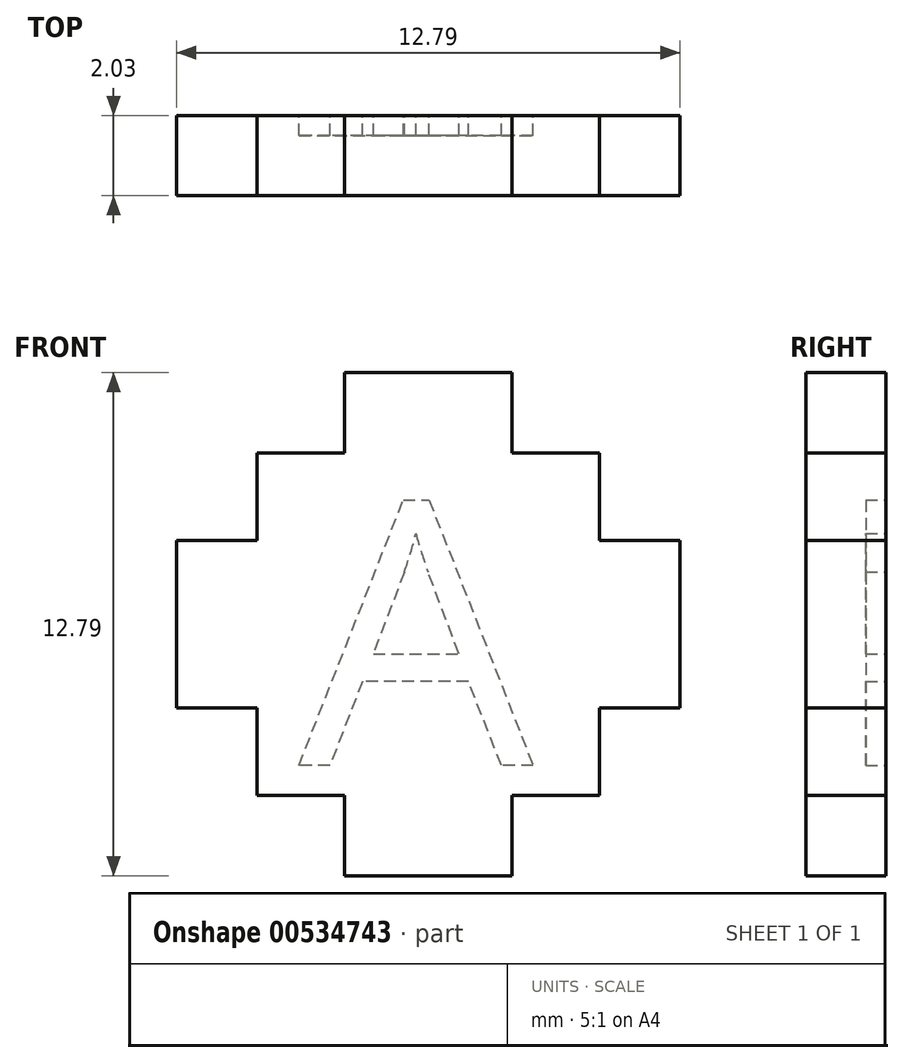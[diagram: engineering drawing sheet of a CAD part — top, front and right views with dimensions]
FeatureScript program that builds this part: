
annotation { "Feature Type Name" : "Feature", "Feature Type Description" : "" }
export const myFeature = defineFeature(function(context is Context, id is Id, definition is map)
    precondition{}
    {
        {
            var Q0;
            Q0=qCreatedBy(makeId("Front.planeOp"),FACE);
            var sketch = newSketch(context, id + "F0", { "sketchPlane" : qUnion([Q0])});
            skLineSegment(sketch, "E0", {"start": v(-17.35, 36.23) * mm, "end": v(-15.22, 36.23) * mm});
            skLineSegment(sketch, "E1", {"start": v(-15.22, 36.23) * mm, "end": v(-15.22, 34.18) * mm});
            skLineSegment(sketch, "E2", {"start": v(-15.22, 34.18) * mm, "end": v(-13, 34.18) * mm});
            skLineSegment(sketch, "E3", {"start": v(-13, 34.18) * mm, "end": v(-13, 31.96) * mm});
            skLineSegment(sketch, "E4", {"start": v(-13, 31.96) * mm, "end": v(-10.95, 31.96) * mm});
            skLineSegment(sketch, "E5", {"start": v(-10.95, 31.96) * mm, "end": v(-10.95, 29.83) * mm});
            skLineSegment(sketch, "E6", {"start": v(-17.35, 36.23) * mm, "end": v(-17.35, 28.94) * mm, "construction": true});
            skLineSegment(sketch, "E7.MirrorCS", {"start": v(-17.35, 36.23) * mm, "end": v(-19.48, 36.23) * mm});
            skLineSegment(sketch, "E8.MirrorCS", {"start": v(-19.48, 36.23) * mm, "end": v(-19.48, 34.18) * mm});
            skLineSegment(sketch, "E9.MirrorCS", {"start": v(-19.48, 34.18) * mm, "end": v(-21.7, 34.18) * mm});
            skLineSegment(sketch, "E10.MirrorCS", {"start": v(-21.7, 34.18) * mm, "end": v(-21.7, 31.96) * mm});
            skLineSegment(sketch, "E11.MirrorCS", {"start": v(-21.7, 31.96) * mm, "end": v(-23.74, 31.96) * mm});
            skLineSegment(sketch, "E12.MirrorCS", {"start": v(-23.74, 31.96) * mm, "end": v(-23.74, 29.83) * mm});
            skLineSegment(sketch, "E13", {"start": v(-23.74, 29.83) * mm, "end": v(-10.95, 29.83) * mm, "construction": true});
            skLineSegment(sketch, "E14.MirrorCS", {"start": v(-23.74, 27.7) * mm, "end": v(-23.74, 29.83) * mm});
            skLineSegment(sketch, "E15.MirrorCS", {"start": v(-21.7, 27.7) * mm, "end": v(-23.74, 27.7) * mm});
            skLineSegment(sketch, "E16.MirrorCS", {"start": v(-21.7, 25.48) * mm, "end": v(-21.7, 27.7) * mm});
            skLineSegment(sketch, "E17.MirrorCS", {"start": v(-19.48, 25.48) * mm, "end": v(-21.7, 25.48) * mm});
            skLineSegment(sketch, "E18.MirrorCS", {"start": v(-19.48, 23.44) * mm, "end": v(-19.48, 25.48) * mm});
            skLineSegment(sketch, "E19.MirrorCS", {"start": v(-17.35, 23.44) * mm, "end": v(-19.48, 23.44) * mm});
            skLineSegment(sketch, "E20.MirrorCS", {"start": v(-17.35, 23.44) * mm, "end": v(-15.22, 23.44) * mm});
            skLineSegment(sketch, "E21.MirrorCS", {"start": v(-15.22, 23.44) * mm, "end": v(-15.22, 25.48) * mm});
            skLineSegment(sketch, "E22.MirrorCS", {"start": v(-15.22, 25.48) * mm, "end": v(-13, 25.48) * mm});
            skLineSegment(sketch, "E23.MirrorCS", {"start": v(-13, 25.48) * mm, "end": v(-13, 27.7) * mm});
            skLineSegment(sketch, "E24.MirrorCS", {"start": v(-13, 27.7) * mm, "end": v(-10.95, 27.7) * mm});
            skLineSegment(sketch, "E25.MirrorCS", {"start": v(-10.95, 27.7) * mm, "end": v(-10.95, 29.83) * mm});
            skSolve(sketch);
        }
        {
            var Q0;
            Q0=makeQuery(id+"F0.imprint","IMPRINT",FACE,{"disambiguationData":[TD([[makeQuery(id+"F0.imprint","IMPRINT",EDGE,{"derivedFrom":sQuery(id+"F0.wireOp",EDGE,"E0")}),-1.0]])]});
            extrude(context, id + "F1", {"entities" : qUnion([Q0]), "depth" : 2.03 * mm, "offsetDistance" : 25 * mm});
        }
        {
            var Q0;
            Q0=qCreatedBy(makeId("Front.planeOp"),FACE);
            var sketch = newSketch(context, id + "F2", { "sketchPlane" : qUnion([Q0])});
            skText(sketch, "E26", { "text": "A", "fontName": "OpenSans-Regular.ttf"});
            const initialGuessF2  = {"E26": [-0.02063, 0.02625, 1, 0, 0.00677]};
            skSetInitialGuess(sketch, initialGuessF2);
            skSolve(sketch);
        }
        {
            var Q0;
            Q0 = qSketchRegion(id + "F2", true);
            extrude(context, id + "F3", {"entities" : qUnion([Q0]), "operationType" : NewBodyOperationType.REMOVE, "depth" : 0.5 * mm, "offsetDistance" : 25.4 * mm});
        }
    });
